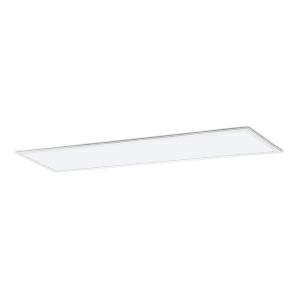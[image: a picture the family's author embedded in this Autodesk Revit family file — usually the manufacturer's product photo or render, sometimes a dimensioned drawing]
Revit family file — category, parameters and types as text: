
# Revit family: dotoo_fit_-_dfe_4000_840_ws_295x1195mm_00815305_a8f6
name_source: partatom
category: Lighting Fixtures
units: mm (PartAtom-declared; Revit-internal decimal feet)

## family parameters
Cut with Voids When Loaded = No
Host = Face
Light Source = No
Part Type = Normal
Room Calculation Point = No
Round Connector Dimension = Use Diameter
Shared = No

## types (1)
- DOTOO.fit - DFE 4000/840/WS/295x1195mm (1 x LED, 4100 lm, 4000K)
    Apparent Load = 30 VA
    Approval mark = CE
    CIE Flux Codes = 66 88 97 100 100
    Color Rendering = 80-89
    Color Temperature = 4000K
    Control Gear = Electronic ballast
    Default Elevation = 1800 mm
    Description = DFE 4000/840|Recessed modular luminaire|light source: LED Cold white   |work equipment: Power supply unit|luminous flux: 4100 lm|light distribution: Direct|direct ratio: approx. 100 %|color rendering index (CRI): >= 80|chromaticity tolerance:  3 SDCM|technology: Switchable|operation: External|luminaire body|material: Sectional aluminium|colour: White|weight (net): approx. 2.9 kg|mains lead: 0.80 m Connector 5 pin|design: Integrated version|glare control: Prism aperture|luminance(L65): <= 3000 cd/m|special features: Direct light component with edge light and light-guide technology for homogenous light exit|
    Frequency = 50 Hz
    Height = 0 mm  [stored 0 ft]
    Lamp = 1 x LED
    Lamp Light Flux = 4100 lm
    Lamp count = 1
    Length = 1195 mm
    Luminous efficacy = 137 lm/W
    Manufacturer = Waldmann
    ModVariant = No
    Model = 00815305
    Mounting Place = Ceiling
    Mounting Type = Recessed
    Number of Poles = 1
    OnlyDefault = Yes
    Power Factor = 1
    Product Name = DOTOO.fit - DFE 4000/840/WS/295x1195mm
    Product group = Recessed luminaire
    ProductGroupID = 4
    Protection Class = Protection class II
    Protection Degree = IP 20
    RLX_Detail_Level = 1
    RLX_Emergency_Light_Flux = 0 lm
    RLX_Emergency_Type = 0
    RLX_Emergency_Type_DB = No
    RlxData = <blob elided: 18261 chars, md5=4357dd69>
    Socket = socket
    Standby Power = 0 W
    System Light Flux = 4100 lm
    System Power = 30 W
    Type Comments = Product without accessories
    Type Image = dfe_dotoofit_1200x300.jpg
    URL = http://relux.com
    VarID = ---
    Voltage = 230 V
    Voltage Range = 220-240 V
    Weight = 0.00 kg
    Width = 295 mm

note: [stored X ft] marks values corroborated as IEEE doubles in the binary element streams (Revit-internal decimal feet)

## geometry (parser evidence)
native form markers: Blend x4, Sweep x10
no freeform markers — native parametric forms only
